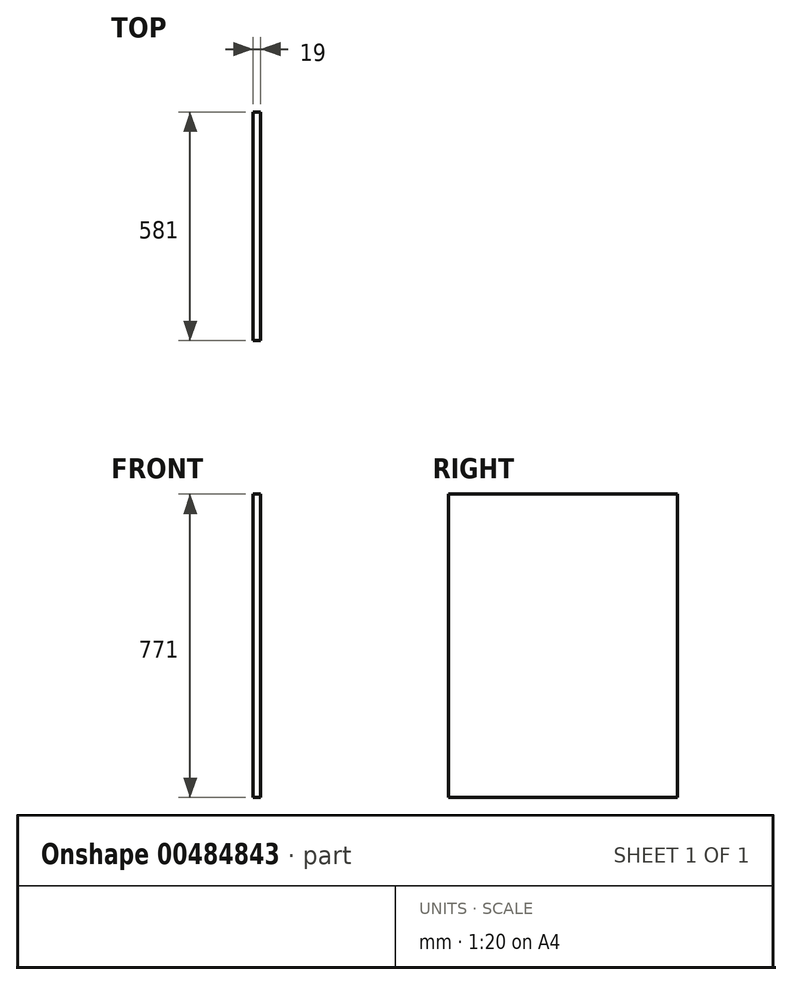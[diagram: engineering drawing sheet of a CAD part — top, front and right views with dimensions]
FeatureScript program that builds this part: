
annotation { "Feature Type Name" : "Feature", "Feature Type Description" : "" }
export const myFeature = defineFeature(function(context is Context, id is Id, definition is map)
    precondition{}
    {
        {
            var Q0;
            Q0=qCreatedBy(makeId("Right.planeOp"),FACE);
            var sketch = newSketch(context, id + "F0", { "sketchPlane" : qUnion([Q0])});
            skLineSegment(sketch, "E0.bottom", {"start": v(-279.42, 566.14) * mm, "end": v(301.58, 566.14) * mm});
            skLineSegment(sketch, "E0.top", {"start": v(-279.42, -204.86) * mm, "end": v(301.58, -204.86) * mm});
            skLineSegment(sketch, "E0.left", {"start": v(-279.42, 566.14) * mm, "end": v(-279.42, -204.86) * mm});
            skLineSegment(sketch, "E0.right", {"start": v(301.58, 566.14) * mm, "end": v(301.58, -204.86) * mm});
            skSolve(sketch);
        }
        {
            var Q0;
            Q0 = qSketchRegion(id + "F0", true);
            extrude(context, id + "F1", {"entities" : qUnion([Q0]), "depth" : 19 * mm});
        }
    });
